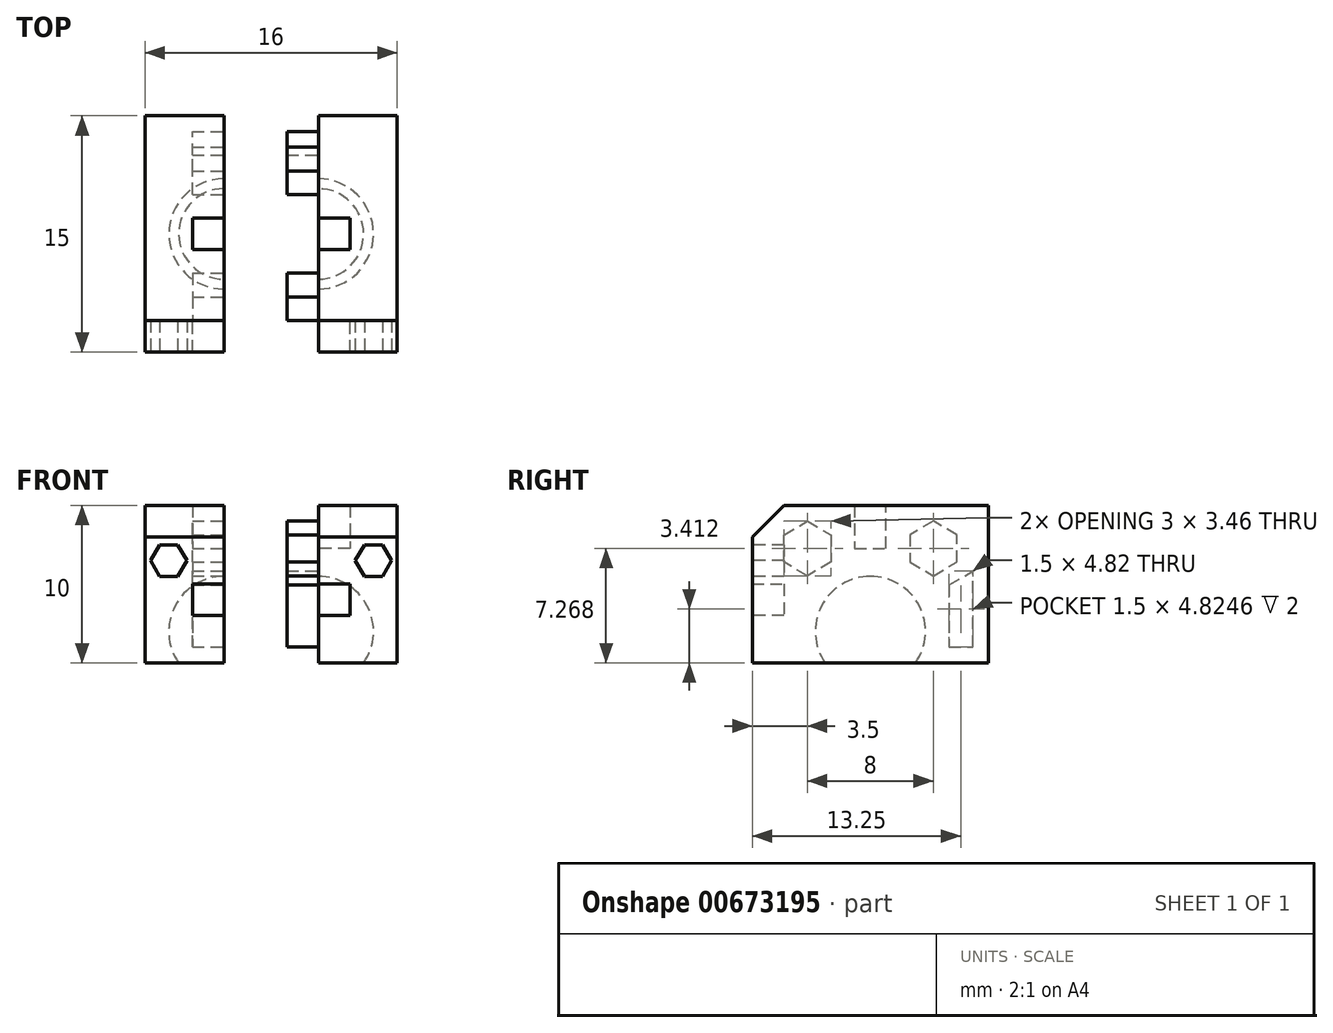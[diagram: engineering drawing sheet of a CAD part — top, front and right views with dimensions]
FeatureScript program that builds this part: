
annotation { "Feature Type Name" : "Feature", "Feature Type Description" : "" }
export const myFeature = defineFeature(function(context is Context, id is Id, definition is map)
    precondition{}
    {
        {
            var Q0;
            Q0=qCreatedBy(makeId("Right.planeOp"),FACE);
            var sketch = newSketch(context, id + "F0", { "sketchPlane" : qUnion([Q0])});
            skLineSegment(sketch, "E0.bottom", {"start": v(0, 0) * mm, "end": v(15, 0) * mm});
            skLineSegment(sketch, "E0.top", {"start": v(0, 10) * mm, "end": v(15, 10) * mm});
            skLineSegment(sketch, "E0.left", {"start": v(0, 0) * mm, "end": v(0, 10) * mm});
            skLineSegment(sketch, "E0.right", {"start": v(15, 0) * mm, "end": v(15, 10) * mm});
            skLineSegment(sketch, "E1", {"start": v(7.5, 0) * mm, "end": v(7.5, 2) * mm, "construction": true});
            skArc(sketch, "E2", {"start": v(7.5, 5.5) * mm, "mid": v(4, 2) * mm, "end": v(7.5, -1.5) * mm});
            skLineSegment(sketch, "E3", {"start": v(7.5, -1.5) * mm, "end": v(7.5, 5.5) * mm});
            skSolve(sketch);
        }
        {
            var Q0;
            Q0=makeQuery(id+"F0.imprint","IMPRINT",FACE,{"disambiguationData":[TD([[makeQuery(id+"F0.imprint","IMPRINT",EDGE,{"derivedFrom":sQuery(id+"F0.wireOp",EDGE,"E0.top")}),-1.0]])]});
            var Q1;
            {var subQ0=sQuery(id+"F0.wireOp",EDGE,"E2");var subQ1=sQuery(id+"F0.wireOp",EDGE,"E0.bottom");var subQ2=makeQuery(id+"F0.imprint","INTERSECT",VERTEX,{"derivedFrom":[subQ1,subQ0]});Q1=makeQuery(id+"F0.imprint","IMPRINT",FACE,{"disambiguationData":[TD([[makeQuery(id+"F0.imprint","IMPRINT",EDGE,{"disambiguationData":[TD([[subQ2,-1.0]])],"derivedFrom":subQ1}),1.0]])]});}
            extrude(context, id + "F1", {"entities" : qUnion([Q0, Q1]), "oppositeDirection" : true, "depth" : 5 * mm});
        }
        {
            var Q0;
            {var subQ0=sQuery(id+"F0.wireOp",EDGE,"E2");var subQ1=sQuery(id+"F0.wireOp",EDGE,"E0.bottom");var subQ2=makeQuery(id+"F0.imprint","INTERSECT",VERTEX,{"derivedFrom":[subQ1,subQ0]});Q0=makeQuery(id+"F0.imprint","IMPRINT",FACE,{"disambiguationData":[TD([[makeQuery(id+"F0.imprint","IMPRINT",EDGE,{"disambiguationData":[TD([[subQ2,-1.0]])],"derivedFrom":subQ1}),1.0]])]});}
            var Q1;
            Q1=sQuery(id+"F0.wireOp",EDGE,"E3");
            revolve(context, id + "F2", {"operationType" : NewBodyOperationType.REMOVE, "entities" : qUnion([Q0]), "axis" : qUnion([Q1]), "revolveType" : RevolveType.FULL, "oppositeDirection" : true});
        }
        {
            var Q0;
            Q0=makeQuery(id+"F1.opExtrude","CAP_FACE",FACE,{"disambiguationData":[OSD([sQuery(id+"F0.wireOp",EDGE,"E0.bottom"),sQuery(id+"F0.wireOp",EDGE,"E0.top"),sQuery(id+"F0.wireOp",EDGE,"E0.left"),sQuery(id+"F0.wireOp",EDGE,"E0.right")])],"isStart":true});
            var sketch = newSketch(context, id + "F3", { "sketchPlane" : qUnion([Q0])});
            skCircle(sketch, "E4.cCircle", {"center": v(3.5, 7.27) * mm, "radius": 1.5 * mm, "construction": true});
            skLineSegment(sketch, "E4.0", {"start": v(2, 6.4) * mm, "end": v(2, 8.13) * mm});
            skLineSegment(sketch, "E4.1", {"start": v(2, 8.13) * mm, "end": v(3.5, 9) * mm});
            skLineSegment(sketch, "E4.2", {"start": v(3.5, 9) * mm, "end": v(5, 8.13) * mm});
            skLineSegment(sketch, "E4.3", {"start": v(5, 8.13) * mm, "end": v(5, 6.4) * mm});
            skLineSegment(sketch, "E4.4", {"start": v(5, 6.4) * mm, "end": v(3.5, 5.54) * mm});
            skLineSegment(sketch, "E4.5", {"start": v(3.5, 5.54) * mm, "end": v(2, 6.4) * mm});
            skPoint(sketch, "E4.0.midPoint", {"position": v(2, 7.27) * mm});
            skLineSegment(sketch, "E5", {"start": v(7.5, 5.5) * mm, "end": v(7.5, 10) * mm, "construction": true});
            skLineSegment(sketch, "E6.MirrorCS", {"start": v(11.5, 5.54) * mm, "end": v(13, 6.4) * mm});
            skLineSegment(sketch, "E7.MirrorCS", {"start": v(10, 6.4) * mm, "end": v(11.5, 5.54) * mm});
            skLineSegment(sketch, "E8.MirrorCS", {"start": v(10, 8.13) * mm, "end": v(10, 6.4) * mm});
            skLineSegment(sketch, "E9.MirrorCS", {"start": v(11.5, 9) * mm, "end": v(10, 8.13) * mm});
            skLineSegment(sketch, "E10.MirrorCS", {"start": v(13, 8.13) * mm, "end": v(11.5, 9) * mm});
            skLineSegment(sketch, "E11.MirrorCS", {"start": v(13, 6.4) * mm, "end": v(13, 8.13) * mm});
            skCircle(sketch, "E12.MirrorC", {"center": v(11.5, 7.27) * mm, "radius": 1.5 * mm, "construction": true});
            skPoint(sketch, "E13.MirrorP", {"position": v(13, 7.27) * mm});
            skSolve(sketch);
        }
        {
            var Q0;
            Q0=qSketchRegion(id+"F3",true);
            extrude(context, id + "F4", {"entities" : qUnion([Q0]), "operationType" : NewBodyOperationType.REMOVE, "oppositeDirection" : true, "depth" : 2 * mm});
        }
        {
            var Q0;
            Q0=makeQuery(id+"F1.opExtrude","CAP_FACE",FACE,{"disambiguationData":[OSD([sQuery(id+"F0.wireOp",EDGE,"E0.bottom"),sQuery(id+"F0.wireOp",EDGE,"E0.top"),sQuery(id+"F0.wireOp",EDGE,"E0.left"),sQuery(id+"F0.wireOp",EDGE,"E0.right")])],"isStart":true});
            var sketch = newSketch(context, id + "F5", { "sketchPlane" : qUnion([Q0])});
            skLineSegment(sketch, "E14", {"start": v(7.5, 10) * mm, "end": v(6.5, 10) * mm, "construction": true});
            skLineSegment(sketch, "E15", {"start": v(6.5, 10) * mm, "end": v(6.5, 7.27) * mm});
            skPoint(sketch, "E15.endSnap0", {"position": v(5, 7.27) * mm});
            skLineSegment(sketch, "E16", {"start": v(6.5, 7.27) * mm, "end": v(8.5, 7.27) * mm});
            skLineSegment(sketch, "E17", {"start": v(8.5, 7.27) * mm, "end": v(8.5, 10) * mm});
            skSolve(sketch);
        }
        {
            var Q0;
            {var subQ0=sQuery(id+"F5.wireOp",EDGE,"E15");Q0=makeQuery(id+"F5.imprint","IMPRINT",FACE,{"disambiguationData":[TD([[makeQuery(id+"F5.imprint","IMPRINT",EDGE,{"derivedFrom":subQ0}),1.0]])]});}
            extrude(context, id + "F6", {"entities" : qUnion([Q0]), "operationType" : NewBodyOperationType.REMOVE, "oppositeDirection" : true, "depth" : 2 * mm});
        }
        {
            var Q0;
            Q0=makeQuery(id+"F1.opExtrude","CAP_FACE",FACE,{"disambiguationData":[OSD([sQuery(id+"F0.wireOp",EDGE,"E0.bottom"),sQuery(id+"F0.wireOp",EDGE,"E0.top"),sQuery(id+"F0.wireOp",EDGE,"E0.left"),sQuery(id+"F0.wireOp",EDGE,"E0.right")])],"isStart":true});
            var sketch = newSketch(context, id + "F7", { "sketchPlane" : qUnion([Q0])});
            skLineSegment(sketch, "E18", {"start": v(0, 5) * mm, "end": v(2, 5) * mm});
            skLineSegment(sketch, "E19", {"start": v(2, 5) * mm, "end": v(2, 3) * mm});
            skLineSegment(sketch, "E20", {"start": v(2, 3) * mm, "end": v(0, 3) * mm});
            skSolve(sketch);
        }
        {
            var Q0;
            {var subQ0=sQuery(id+"F7.wireOp",EDGE,"E18");Q0=makeQuery(id+"F7.imprint","IMPRINT",FACE,{"disambiguationData":[TD([[makeQuery(id+"F7.imprint","IMPRINT",EDGE,{"derivedFrom":subQ0}),-1.0]])]});}
            extrude(context, id + "F8", {"entities" : qUnion([Q0]), "operationType" : NewBodyOperationType.REMOVE, "oppositeDirection" : true, "depth" : 2 * mm});
        }
        {
            var Q0;
            Q0=makeQuery(id+"F1.opExtrude","SWEPT_EDGE",EDGE,{"disambiguationData":[OSD([sQuery(id+"F0.wireOp",EDGE,"E0.top"),sQuery(id+"F0.wireOp",EDGE,"E0.left")])]});
            chamfer(context, id + "F9", {"entities" : qUnion([Q0]), "width" : 2 * mm, "tangentPropagation" : true});
        }
        {
            var Q0;
            Q0=makeQuery(id+"F1.opExtrude","CAP_FACE",FACE,{"disambiguationData":[OSD([sQuery(id+"F0.wireOp",EDGE,"E0.bottom"),sQuery(id+"F0.wireOp",EDGE,"E0.top"),sQuery(id+"F0.wireOp",EDGE,"E0.left"),sQuery(id+"F0.wireOp",EDGE,"E0.right")])],"isStart":true});
            var sketch = newSketch(context, id + "F10", { "sketchPlane" : qUnion([Q0])});
            skLineSegment(sketch, "E21", {"start": v(11.5, 9) * mm, "end": v(15, 9) * mm, "construction": true});
            skLineSegment(sketch, "E22", {"start": v(11.5, 5.54) * mm, "end": v(11.5, 0) * mm, "construction": true});
            skLineSegment(sketch, "E23", {"start": v(11.5, 0) * mm, "end": v(15, 0) * mm, "construction": true});
            skLineSegment(sketch, "E24", {"start": v(15, 0) * mm, "end": v(15, 9) * mm, "construction": true});
            skLineSegment(sketch, "E25.0", {"start": v(12.5, 1) * mm, "end": v(14, 1) * mm});
            skLineSegment(sketch, "E25.3", {"start": v(14, 1) * mm, "end": v(14, 5.82) * mm});
            skLineSegment(sketch, "E25.4", {"start": v(12.5, 4.96) * mm, "end": v(14, 5.82) * mm});
            skLineSegment(sketch, "E25.5", {"start": v(12.5, 4.96) * mm, "end": v(12.5, 1) * mm});
            skSolve(sketch);
        }
        {
            var Q0;
            Q0=makeQuery(id+"F10.imprint","IMPRINT",FACE,{"disambiguationData":[TD([[makeQuery(id+"F10.imprint","IMPRINT",EDGE,{"derivedFrom":sQuery(id+"F10.wireOp",EDGE,"E25.0")}),1.0]])]});
            extrude(context, id + "F11", {"entities" : qUnion([Q0]), "operationType" : NewBodyOperationType.REMOVE, "oppositeDirection" : true, "depth" : 2 * mm});
        }
        {
            var Q0;
            Q0=makeQuery(id+"F1.opExtrude","SWEPT_FACE",FACE,{"disambiguationData":[OSD([sQuery(id+"F0.wireOp",EDGE,"E0.left")])]});
            var sketch = newSketch(context, id + "F12", { "sketchPlane" : qUnion([Q0])});
            skLineSegment(sketch, "E26", {"start": v(-2, 5) * mm, "end": v(-5, 5) * mm});
            skLineSegment(sketch, "E27", {"start": v(-2, 3) * mm, "end": v(-2, 2) * mm});
            skLineSegment(sketch, "E28", {"start": v(-2, 2) * mm, "end": v(0, 2) * mm});
            skLineSegment(sketch, "E29", {"start": v(-2, 5) * mm, "end": v(-2, 8) * mm});
            skLineSegment(sketch, "E30", {"start": v(-5, 1.5) * mm, "end": v(-5, 0) * mm, "construction": true});
            skLineSegment(sketch, "E31", {"start": v(-5, 0) * mm, "end": v(0, 0) * mm, "construction": true});
            skLineSegment(sketch, "E32", {"start": v(0, 0) * mm, "end": v(0, 2) * mm, "construction": true});
            skLineSegment(sketch, "E33", {"start": v(-5, 5) * mm, "end": v(-5, 8) * mm, "construction": true});
            skLineSegment(sketch, "E34", {"start": v(-5, 8) * mm, "end": v(-2, 8) * mm, "construction": true});
            skCircle(sketch, "E35.cCircle", {"center": v(-3.5, 6.5) * mm, "radius": 1 * mm, "construction": true});
            skPoint(sketch, "E35.cCircle.centerSnap0", {"position": v(-2, 6.5) * mm});
            skPoint(sketch, "E35.cCircle.centerSnap1", {"position": v(-3.5, 8) * mm});
            skPoint(sketch, "E35.cCircle.perimeterSnap0", {"position": v(-3.5, 8) * mm});
            skLineSegment(sketch, "E35.0", {"start": v(-2.92, 5.5) * mm, "end": v(-4.08, 5.5) * mm});
            skLineSegment(sketch, "E35.1", {"start": v(-4.08, 5.5) * mm, "end": v(-4.65, 6.5) * mm});
            skLineSegment(sketch, "E35.2", {"start": v(-4.65, 6.5) * mm, "end": v(-4.08, 7.5) * mm});
            skLineSegment(sketch, "E35.3", {"start": v(-4.08, 7.5) * mm, "end": v(-2.92, 7.5) * mm});
            skLineSegment(sketch, "E35.4", {"start": v(-2.92, 7.5) * mm, "end": v(-2.35, 6.5) * mm});
            skLineSegment(sketch, "E35.5", {"start": v(-2.35, 6.5) * mm, "end": v(-2.92, 5.5) * mm});
            skPoint(sketch, "E35.0.midPoint", {"position": v(-3.5, 5.5) * mm});
            skPoint(sketch, "E35.0.midPoint.positionSnap0", {"position": v(-3.5, 8) * mm});
            skLineSegment(sketch, "E36", {"start": v(-2, 2) * mm, "end": v(-3.5, 2) * mm});
            skLineSegment(sketch, "E37", {"start": v(-3.5, 2) * mm, "end": v(-5, 1.5) * mm});
            skPoint(sketch, "E38.orphan", {"position": v(-5, 3) * mm});
            skSolve(sketch);
        }
        {
            var Q0;
            Q0=makeQuery(id+"F12.imprint","IMPRINT",FACE,{"disambiguationData":[TD([[makeQuery(id+"F12.imprint","IMPRINT",EDGE,{"derivedFrom":sQuery(id+"F12.wireOp",EDGE,"E35.0")}),-1.0]])]});
            extrude(context, id + "F13", {"entities" : qUnion([Q0]), "operationType" : NewBodyOperationType.REMOVE, "oppositeDirection" : true, "depth" : 2 * mm});
        }
        {
            var Q0;
            Q0=qCreatedBy(makeId("Right.planeOp"),FACE);
            cPlane(context, id + "F14", {"entities" : qUnion([Q0]), "cplaneType" : CPlaneType.OFFSET, "offset" : 3 * mm, "width" : 150 * mm, "height" : 150 * mm});
        }
        {
            var Q0;
            Q0=makeQuery(id+"F1.opExtrude","SWEPT_BODY",BODY,{"disambiguationData":[OSD([sQuery(id+"F0.wireOp",EDGE,"E0.bottom"),sQuery(id+"F0.wireOp",EDGE,"E0.top"),sQuery(id+"F0.wireOp",EDGE,"E0.left"),sQuery(id+"F0.wireOp",EDGE,"E0.right")])]});
            var Q1;
            Q1=qCreatedBy(id+"F14.planeOp",FACE);
            mirror(context, id + "F15", {"entities" : qUnion([Q0]), "mirrorPlane" : qUnion([Q1])});
        }
        {
            var Q0;
            Q0=makeQuery(id+"F15.opPattern","COPY",FACE,{"derivedFrom":makeQuery(id+"F4.boolean.opBoolean","COPY",FACE,{"derivedFrom":makeQuery(id+"F4.opExtrude","CAP_FACE",FACE,{"disambiguationData":[OSD([sQuery(id+"F3.wireOp",EDGE,"E4.0"),sQuery(id+"F3.wireOp",EDGE,"E4.1"),sQuery(id+"F3.wireOp",EDGE,"E4.2"),sQuery(id+"F3.wireOp",EDGE,"E4.3"),sQuery(id+"F3.wireOp",EDGE,"E4.4"),sQuery(id+"F3.wireOp",EDGE,"E4.5")])],"isStart":false})}),"instanceName":"1"});
            var Q1;
            Q1=makeQuery(id+"F15.opPattern","COPY",FACE,{"derivedFrom":makeQuery(id+"F4.boolean.opBoolean","COPY",FACE,{"derivedFrom":makeQuery(id+"F4.opExtrude","CAP_FACE",FACE,{"disambiguationData":[OSD([sQuery(id+"F3.wireOp",EDGE,"E6.MirrorCS"),sQuery(id+"F3.wireOp",EDGE,"E7.MirrorCS"),sQuery(id+"F3.wireOp",EDGE,"E8.MirrorCS"),sQuery(id+"F3.wireOp",EDGE,"E9.MirrorCS"),sQuery(id+"F3.wireOp",EDGE,"E10.MirrorCS"),sQuery(id+"F3.wireOp",EDGE,"E11.MirrorCS")])],"isStart":false})}),"instanceName":"1"});
            var Q2;
            Q2=makeQuery(id+"F15.opPattern","COPY",FACE,{"derivedFrom":makeQuery(id+"F11.boolean.opBoolean","COPY",FACE,{"derivedFrom":makeQuery(id+"F11.opExtrude","CAP_FACE",FACE,{"disambiguationData":[OSD([sQuery(id+"F10.wireOp",EDGE,"E25.0"),sQuery(id+"F10.wireOp",EDGE,"E25.3"),sQuery(id+"F10.wireOp",EDGE,"E25.4"),sQuery(id+"F10.wireOp",EDGE,"E25.5")])],"isStart":false})}),"instanceName":"1"});
            extrude(context, id + "F16", {"entities" : qUnion([Q0, Q1, Q2]), "operationType" : NewBodyOperationType.ADD, "depth" : 4 * mm});
        }
    });
